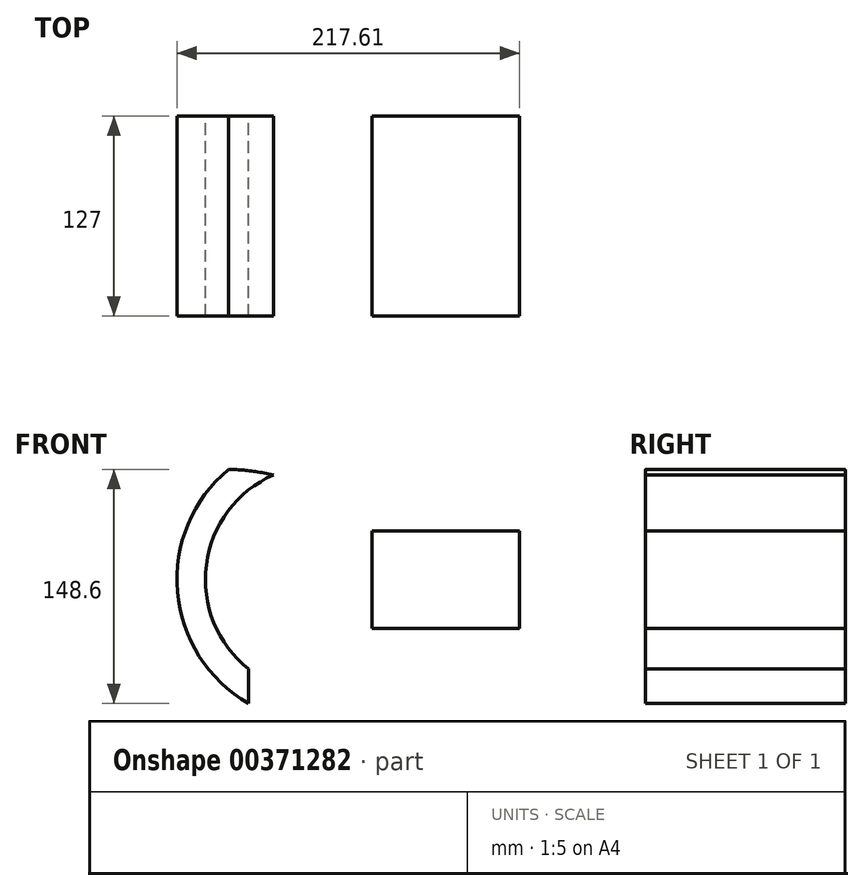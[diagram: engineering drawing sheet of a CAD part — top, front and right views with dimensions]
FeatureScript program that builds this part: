
annotation { "Feature Type Name" : "Feature", "Feature Type Description" : "" }
export const myFeature = defineFeature(function(context is Context, id is Id, definition is map)
    precondition{}
    {
        {
            var Q0;
            Q0=qCreatedBy(makeId("Front.planeOp"),FACE);
            var sketch = newSketch(context, id + "F0", { "sketchPlane" : qUnion([Q0])});
            skLineSegment(sketch, "E0.bottom", {"start": v(-97.98, 84.92) * mm, "end": v(-21.78, 84.92) * mm});
            skLineSegment(sketch, "E0.top", {"start": v(-97.98, -64.52) * mm, "end": v(-21.78, -64.52) * mm});
            skLineSegment(sketch, "E0.left", {"start": v(-97.98, 84.92) * mm, "end": v(-97.98, -64.52) * mm});
            skLineSegment(sketch, "E0.right", {"start": v(-21.78, 84.92) * mm, "end": v(-21.78, -64.52) * mm});
            skLineSegment(sketch, "E1.bottom", {"start": v(56.51, 37.53) * mm, "end": v(150.26, 37.53) * mm});
            skLineSegment(sketch, "E1.top", {"start": v(56.51, 99.55) * mm, "end": v(150.26, 99.55) * mm});
            skLineSegment(sketch, "E1.left", {"start": v(56.51, 37.53) * mm, "end": v(56.51, 99.55) * mm});
            skLineSegment(sketch, "E1.right", {"start": v(150.26, 37.53) * mm, "end": v(150.26, 99.55) * mm});
            skLineSegment(sketch, "E2", {"start": v(-21.78, 68.7) * mm, "end": v(-21.78, 84.92) * mm});
            skArc(sketch, "E3", {"start": v(-21.78, 68.7) * mm, "mid": v(6.87, 110.78) * mm, "end": v(56.51, 99.55) * mm});
            skArc(sketch, "E4.0", {"start": v(-15.43, 34.82) * mm, "mid": v(-11.1, 107) * mm, "end": v(61.16, 103.88) * mm});
            skLineSegment(sketch, "E4.1", {"start": v(-15.43, 34.82) * mm, "end": v(-15.43, 84.92) * mm});
            skArc(sketch, "E5.0", {"start": v(-5.25, 14.03) * mm, "mid": v(-25.65, 106.17) * mm, "end": v(68.6, 110.82) * mm});
            skLineSegment(sketch, "E5.1", {"start": v(-5.25, 14.03) * mm, "end": v(-5.25, 84.92) * mm});
            skArc(sketch, "E6.0", {"start": v(5.67, -1.75) * mm, "mid": v(-39.11, 105.68) * mm, "end": v(76.59, 118.26) * mm});
            skLineSegment(sketch, "E6.1", {"start": v(5.67, -1.75) * mm, "end": v(5.67, 84.92) * mm});
            skArc(sketch, "E7.0", {"start": v(23.8, -22.08) * mm, "mid": v(-59.88, 104.75) * mm, "end": v(89.84, 130.62) * mm});
            skLineSegment(sketch, "E7.1", {"start": v(23.8, -22.08) * mm, "end": v(23.8, 84.92) * mm});
            skFitSpline(sketch, "E8", {"points": [v(-97.98, 84.92) * mm, v(68.6, 110.82) * mm], "startDerivative": vector(166.58, 25.9) * mm, "endDerivative": vector(542.38, -215.29) * mm});
            skFitSpline(sketch, "E9", {"points": [v(97.98, -34.59) * mm, v(117.89, -98) * mm, v(175.77, -22.05) * mm], "startDerivative": vector(-206.72, -338.04) * mm, "endDerivative": vector(706.62, 259.7) * mm});
            skFitSpline(sketch, "E10", {"points": [v(175.77, -22.05) * mm, v(150.26, 37.53) * mm], "startDerivative": vector(-23.23, 236.71) * mm, "endDerivative": vector(-59.96, 385.58) * mm});
            skFitSpline(sketch, "E11", {"points": [v(175.77, -22.05) * mm, v(138.53, 0) * mm], "startDerivative": vector(-171.45, -40.93) * mm, "endDerivative": vector(-100.66, -152.85) * mm});
            skSolve(sketch);
        }
        {
            var Q0;
            {var subQ0=sQuery(id+"F0.wireOp",EDGE,"E7.0");var subQ1=sQuery(id+"F0.wireOp",EDGE,"E0.bottom");var subQ2=makeQuery(id+"F0.imprint","INTERSECT",VERTEX,{"derivedFrom":[subQ1,subQ0]});Q0=makeQuery(id+"F0.imprint","IMPRINT",FACE,{"disambiguationData":[TD([[makeQuery(id+"F0.imprint","IMPRINT",EDGE,{"disambiguationData":[TD([[subQ2,-1.0]])],"derivedFrom":subQ1}),-1.0]])]});}
            var Q1;
            {var subQ0=sQuery(id+"F0.wireOp",EDGE,"E7.0");var subQ1=sQuery(id+"F0.wireOp",EDGE,"E0.bottom");var subQ2=makeQuery(id+"F0.imprint","INTERSECT",VERTEX,{"derivedFrom":[subQ1,subQ0]});Q1=makeQuery(id+"F0.imprint","IMPRINT",FACE,{"disambiguationData":[TD([[makeQuery(id+"F0.imprint","IMPRINT",EDGE,{"disambiguationData":[TD([[subQ2,-1.0]])],"derivedFrom":subQ1}),1.0]])]});}
            var Q2;
            Q2=makeQuery(id+"F0.imprint","IMPRINT",FACE,{"disambiguationData":[TD([[makeQuery(id+"F0.imprint","IMPRINT",EDGE,{"derivedFrom":sQuery(id+"F0.wireOp",EDGE,"E1.bottom")}),1.0]])]});
            extrude(context, id + "F1", {"entities" : qUnion([Q0, Q1, Q2]), "depth" : 127 * mm});
        }
    });
